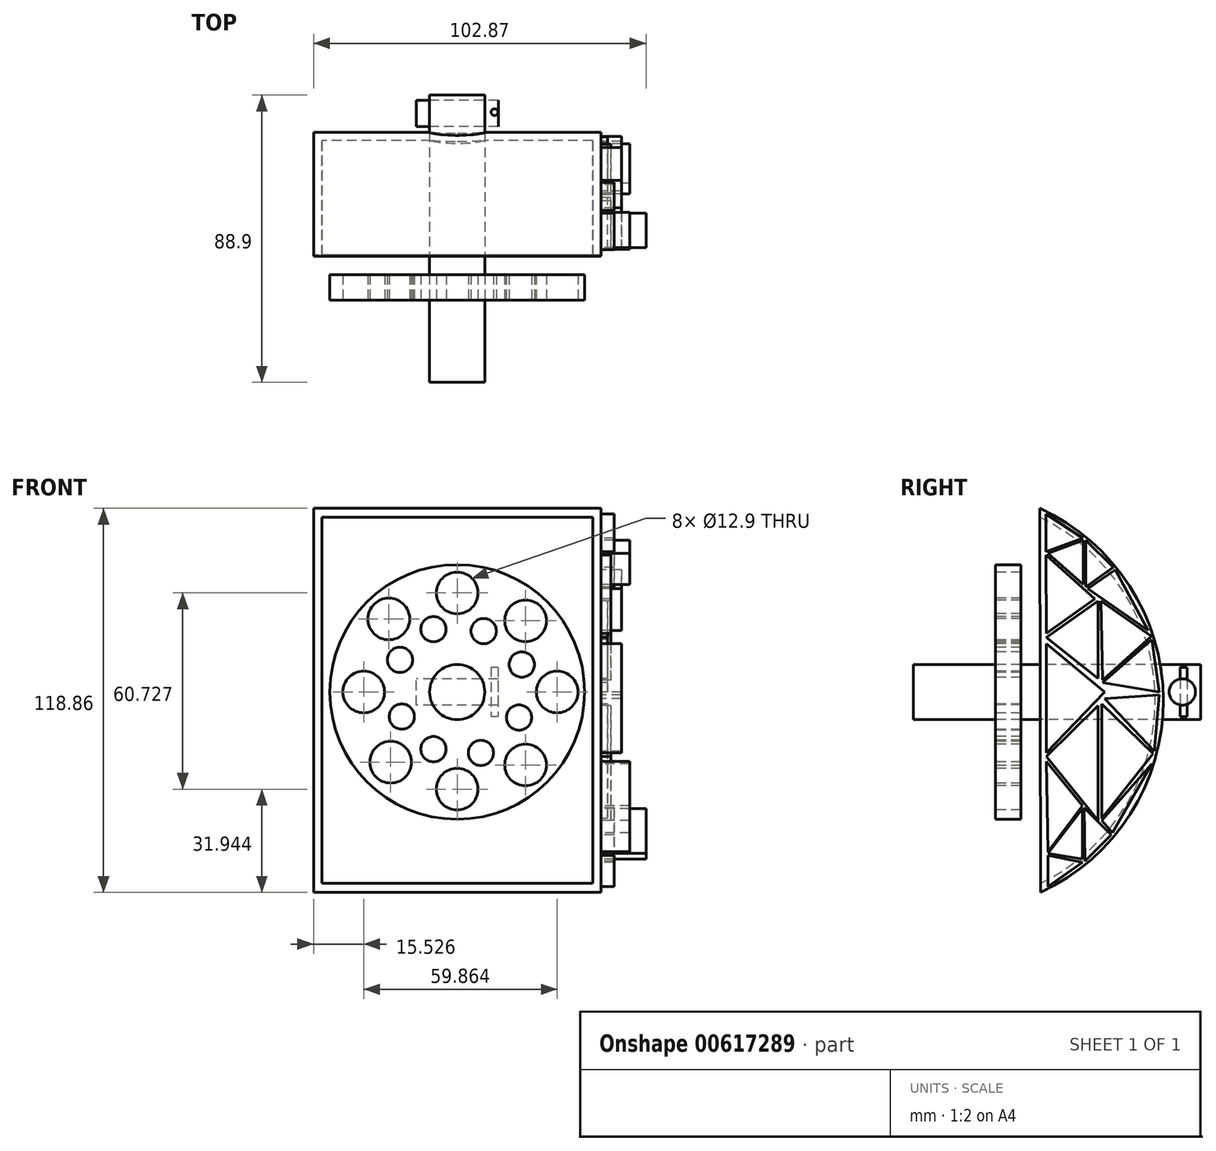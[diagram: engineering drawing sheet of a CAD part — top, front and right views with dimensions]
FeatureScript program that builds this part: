
annotation { "Feature Type Name" : "Feature", "Feature Type Description" : "" }
export const myFeature = defineFeature(function(context is Context, id is Id, definition is map)
    precondition{}
    {
        {
            var Q0;
            Q0=qCreatedBy(makeId("Right.planeOp"),FACE);
            var sketch = newSketch(context, id + "F0", { "sketchPlane" : qUnion([Q0])});
            skArc(sketch, "E0", {"start": v(13.96, -62.02) * mm, "mid": v(51.96, -2.5) * mm, "end": v(13.67, 56.84) * mm});
            skLineSegment(sketch, "E1", {"start": v(13.67, 56.84) * mm, "end": v(13.96, -62.02) * mm});
            skSolve(sketch);
        }
        {
            var Q0;
            Q0 = qSketchRegion(id + "F0", true);
            extrude(context, id + "F1", {"entities" : qUnion([Q0]), "endBound" : BoundingType.SYMMETRIC, "depth" : 88.9 * mm, "offsetDistance" : 25.4 * mm});
        }
        {
            var Q0;
            Q0=makeQuery(id+"F1.opExtrude","SWEPT_FACE",FACE,{"disambiguationData":[OSD([sQuery(id+"F0.wireOp",EDGE,"E1")])]});
            shell(context, id + "F2", {"entities" : qUnion([Q0]), "thickness" : 2.54 * mm});
        }
        {
            var Q0;
            Q0=makeQuery(id+"F1.opExtrude","CAP_FACE",FACE,{"disambiguationData":[OSD([sQuery(id+"F0.wireOp",EDGE,"E0"),sQuery(id+"F0.wireOp",EDGE,"E1")])],"isStart":false});
            var sketch = newSketch(context, id + "F3", { "sketchPlane" : qUnion([Q0])});
            skLineSegment(sketch, "E2", {"start": v(15.74, 14.93) * mm, "end": v(15.82, -18.86) * mm});
            skLineSegment(sketch, "E3", {"start": v(15.82, -18.86) * mm, "end": v(33.85, 0) * mm});
            skLineSegment(sketch, "E4", {"start": v(33.85, 0) * mm, "end": v(15.74, 14.93) * mm});
            skLineSegment(sketch, "E5", {"start": v(15.74, 18.18) * mm, "end": v(15.68, 42.4) * mm});
            skLineSegment(sketch, "E6", {"start": v(15.68, 42.4) * mm, "end": v(30.8, 28.76) * mm});
            skLineSegment(sketch, "E7", {"start": v(30.8, 28.76) * mm, "end": v(15.74, 18.18) * mm});
            skLineSegment(sketch, "E8", {"start": v(15.74, 16.92) * mm, "end": v(31.8, 28.21) * mm});
            skLineSegment(sketch, "E9", {"start": v(31.8, 28.21) * mm, "end": v(31.8, 4.19) * mm});
            skLineSegment(sketch, "E10", {"start": v(31.8, 4.19) * mm, "end": v(15.74, 16.92) * mm});
            skLineSegment(sketch, "E11", {"start": v(15.68, 43.45) * mm, "end": v(15.68, 55.04) * mm});
            skLineSegment(sketch, "E12", {"start": v(15.68, 55.04) * mm, "end": v(27, 47.62) * mm});
            skLineSegment(sketch, "E13", {"start": v(27, 47.62) * mm, "end": v(15.68, 43.45) * mm});
            skLineSegment(sketch, "E14", {"start": v(16.32, 42.93) * mm, "end": v(27.2, 46.95) * mm});
            skLineSegment(sketch, "E15", {"start": v(16.32, 42.93) * mm, "end": v(27.2, 33.3) * mm});
            skLineSegment(sketch, "E16", {"start": v(27.2, 33.3) * mm, "end": v(27.2, 46.95) * mm});
            skLineSegment(sketch, "E17", {"start": v(27.89, 46.95) * mm, "end": v(27.89, 32.54) * mm});
            skLineSegment(sketch, "E18", {"start": v(27.89, 32.54) * mm, "end": v(36.49, 38.62) * mm});
            skLineSegment(sketch, "E19", {"start": v(36.49, 38.62) * mm, "end": v(27.89, 46.95) * mm});
            skLineSegment(sketch, "E20", {"start": v(15.82, -20.01) * mm, "end": v(31.8, -4.22) * mm});
            skLineSegment(sketch, "E21", {"start": v(31.8, -4.22) * mm, "end": v(31.8, -39.8) * mm});
            skLineSegment(sketch, "E22", {"start": v(31.8, -39.8) * mm, "end": v(15.82, -20.01) * mm});
            skLineSegment(sketch, "E23", {"start": v(15.82, -21.43) * mm, "end": v(16.32, -49.42) * mm});
            skLineSegment(sketch, "E24", {"start": v(15.82, -21.43) * mm, "end": v(26.9, -35.15) * mm});
            skLineSegment(sketch, "E25", {"start": v(26.9, -35.15) * mm, "end": v(16.32, -49.42) * mm});
            skLineSegment(sketch, "E26", {"start": v(16.32, -50.52) * mm, "end": v(16.32, -60.2) * mm});
            skLineSegment(sketch, "E27", {"start": v(16.32, -60.2) * mm, "end": v(26.9, -52.7) * mm});
            skLineSegment(sketch, "E28", {"start": v(26.9, -52.7) * mm, "end": v(16.32, -50.52) * mm});
            skLineSegment(sketch, "E29", {"start": v(16.32, -49.9) * mm, "end": v(26.9, -36.05) * mm});
            skLineSegment(sketch, "E30", {"start": v(26.9, -36.05) * mm, "end": v(26.9, -51.68) * mm});
            skLineSegment(sketch, "E31", {"start": v(16.32, -49.9) * mm, "end": v(26.9, -51.68) * mm});
            skLineSegment(sketch, "E32", {"start": v(27.45, -35.79) * mm, "end": v(27.74, -52.3) * mm});
            skLineSegment(sketch, "E33", {"start": v(27.74, -52.3) * mm, "end": v(35.8, -44.17) * mm});
            skLineSegment(sketch, "E34", {"start": v(35.8, -44.17) * mm, "end": v(27.45, -35.79) * mm});
            skLineSegment(sketch, "E35", {"start": v(32.7, 28.21) * mm, "end": v(33.12, 3.7) * mm});
            skLineSegment(sketch, "E36", {"start": v(33.12, 3.7) * mm, "end": v(48.31, 17.27) * mm});
            skLineSegment(sketch, "E37", {"start": v(48.31, 17.27) * mm, "end": v(32.7, 28.21) * mm});
            skLineSegment(sketch, "E38", {"start": v(28.62, 32.03) * mm, "end": v(47.23, 19) * mm});
            skLineSegment(sketch, "E39", {"start": v(47.23, 19) * mm, "end": v(37.12, 37.78) * mm});
            skLineSegment(sketch, "E40", {"start": v(37.12, 37.78) * mm, "end": v(28.62, 32.03) * mm});
            skLineSegment(sketch, "E41", {"start": v(32.9, -3.7) * mm, "end": v(32.9, -39.13) * mm});
            skPoint(sketch, "E41.startSnap0", {"position": v(32.9, 15.95) * mm});
            skLineSegment(sketch, "E42", {"start": v(32.9, -39.13) * mm, "end": v(48.83, -19.04) * mm});
            skLineSegment(sketch, "E43", {"start": v(48.83, -19.04) * mm, "end": v(32.9, -3.7) * mm});
            skLineSegment(sketch, "E44", {"start": v(32.9, -39.83) * mm, "end": v(36.2, -43.52) * mm});
            skLineSegment(sketch, "E45", {"start": v(36.2, -43.52) * mm, "end": v(48.43, -22.25) * mm});
            skLineSegment(sketch, "E46", {"start": v(48.43, -22.25) * mm, "end": v(32.9, -39.83) * mm});
            skLineSegment(sketch, "E47", {"start": v(33.12, 2.9) * mm, "end": v(48.39, 16.17) * mm});
            skLineSegment(sketch, "E48", {"start": v(48.39, 16.17) * mm, "end": v(50.63, 0) * mm});
            skLineSegment(sketch, "E49", {"start": v(50.63, 0) * mm, "end": v(33.12, 2.9) * mm});
            skLineSegment(sketch, "E50", {"start": v(33.85, -2.04) * mm, "end": v(50.69, -0.9) * mm});
            skLineSegment(sketch, "E51", {"start": v(50.69, -0.9) * mm, "end": v(49.11, -18.32) * mm});
            skLineSegment(sketch, "E52", {"start": v(49.11, -18.32) * mm, "end": v(33.85, -2.04) * mm});
            skSolve(sketch);
        }
        {
            var Q0;
            Q0=makeQuery(id+"F3.imprint","IMPRINT",FACE,{"disambiguationData":[TD([[makeQuery(id+"F3.imprint","IMPRINT",EDGE,{"derivedFrom":sQuery(id+"F3.wireOp",EDGE,"E35")}),1.0]])]});
            var Q1;
            Q1=makeQuery(id+"F3.imprint","IMPRINT",FACE,{"disambiguationData":[TD([[makeQuery(id+"F3.imprint","IMPRINT",EDGE,{"derivedFrom":sQuery(id+"F3.wireOp",EDGE,"E5")}),-1.0]])]});
            var Q2;
            Q2=makeQuery(id+"F3.imprint","IMPRINT",FACE,{"disambiguationData":[TD([[makeQuery(id+"F3.imprint","IMPRINT",EDGE,{"derivedFrom":sQuery(id+"F3.wireOp",EDGE,"E20")}),-1.0]])]});
            var Q3;
            Q3=makeQuery(id+"F3.imprint","IMPRINT",FACE,{"disambiguationData":[TD([[makeQuery(id+"F3.imprint","IMPRINT",EDGE,{"derivedFrom":sQuery(id+"F3.wireOp",EDGE,"E50")}),-1.0]])]});
            extrude(context, id + "F4", {"entities" : qUnion([Q0, Q1, Q2, Q3]), "operationType" : NewBodyOperationType.ADD, "depth" : 3.05 * mm, "offsetDistance" : 25.4 * mm});
        }
        {
            var Q0;
            Q0=makeQuery(id+"F3.imprint","IMPRINT",FACE,{"disambiguationData":[TD([[makeQuery(id+"F3.imprint","IMPRINT",EDGE,{"derivedFrom":sQuery(id+"F3.wireOp",EDGE,"E8")}),-1.0]])]});
            var Q1;
            Q1=makeQuery(id+"F3.imprint","IMPRINT",FACE,{"disambiguationData":[TD([[makeQuery(id+"F3.imprint","IMPRINT",EDGE,{"derivedFrom":sQuery(id+"F3.wireOp",EDGE,"E47")}),-1.0]])]});
            var Q2;
            Q2=makeQuery(id+"F3.imprint","IMPRINT",FACE,{"disambiguationData":[TD([[makeQuery(id+"F3.imprint","IMPRINT",EDGE,{"derivedFrom":sQuery(id+"F3.wireOp",EDGE,"E41")}),1.0]])]});
            extrude(context, id + "F5", {"entities" : qUnion([Q0, Q1, Q2]), "operationType" : NewBodyOperationType.ADD, "depth" : 2.03 * mm, "offsetDistance" : 25.4 * mm});
        }
        {
            var Q0;
            Q0=qCreatedBy(makeId("Front.planeOp"),FACE);
            var sketch = newSketch(context, id + "F6", { "sketchPlane" : qUnion([Q0])});
            skCircle(sketch, "E53", {"center": v(0, 0) * mm, "radius": 8.59 * mm});
            skSolve(sketch);
        }
        {
            var Q0;
            Q0 = qSketchRegion(id + "F6", true);
            extrude(context, id + "F7", {"entities" : qUnion([Q0]), "operationType" : NewBodyOperationType.REMOVE, "oppositeDirection" : true, "depth" : 111.76 * mm, "offsetDistance" : 25.4 * mm});
        }
        {
            var Q0;
            Q0=qCreatedBy(makeId("Front.planeOp"),FACE);
            var sketch = newSketch(context, id + "F8", { "sketchPlane" : qUnion([Q0])});
            skCircle(sketch, "E54", {"center": v(0, 0) * mm, "radius": 39.4 * mm});
            skCircle(sketch, "E55", {"center": v(0, -30.08) * mm, "radius": 6.45 * mm});
            skCircle(sketch, "E56", {"center": v(30.94, 0) * mm, "radius": 6.45 * mm});
            skCircle(sketch, "E57", {"center": v(0, 30.65) * mm, "radius": 6.45 * mm});
            skCircle(sketch, "E58", {"center": v(-28.92, 0) * mm, "radius": 6.45 * mm});
            skCircle(sketch, "E59", {"center": v(21.15, -22.6) * mm, "radius": 6.45 * mm});
            skCircle(sketch, "E60", {"center": v(-20.58, -21.73) * mm, "radius": 6.45 * mm});
            skCircle(sketch, "E61", {"center": v(-21.15, 22.6) * mm, "radius": 6.45 * mm});
            skCircle(sketch, "E62", {"center": v(21.15, 22.02) * mm, "radius": 6.45 * mm});
            skCircle(sketch, "E63", {"center": v(-7.34, 19.43) * mm, "radius": 3.91 * mm});
            skCircle(sketch, "E64", {"center": v(8.2, 18.85) * mm, "radius": 3.91 * mm});
            skCircle(sketch, "E65", {"center": v(20, 8.5) * mm, "radius": 3.91 * mm});
            skCircle(sketch, "E66", {"center": v(19.14, -7.91) * mm, "radius": 3.91 * mm});
            skCircle(sketch, "E67", {"center": v(7.34, -18.85) * mm, "radius": 3.91 * mm});
            skCircle(sketch, "E68", {"center": v(-17.12, -7.63) * mm, "radius": 3.91 * mm});
            skCircle(sketch, "E69", {"center": v(-17.7, 9.93) * mm, "radius": 3.91 * mm});
            skCircle(sketch, "E70", {"center": v(-7.34, -17.7) * mm, "radius": 3.91 * mm});
            skCircle(sketch, "E71", {"center": v(0, 0) * mm, "radius": 8.54 * mm});
            skSolve(sketch);
        }
        {
            var Q0;
            Q0 = qSketchRegion(id + "F8", true);
            extrude(context, id + "F9", {"entities" : qUnion([Q0]), "oppositeDirection" : true, "depth" : 7.87 * mm, "offsetDistance" : 25.4 * mm});
        }
        {
            var Q0;
            Q0=makeQuery(id+"F3.imprint","IMPRINT",FACE,{"disambiguationData":[TD([[makeQuery(id+"F3.imprint","IMPRINT",EDGE,{"derivedFrom":sQuery(id+"F3.wireOp",EDGE,"E17")}),1.0]])]});
            var Q1;
            Q1=makeQuery(id+"F3.imprint","IMPRINT",FACE,{"disambiguationData":[TD([[makeQuery(id+"F3.imprint","IMPRINT",EDGE,{"derivedFrom":sQuery(id+"F3.wireOp",EDGE,"E32")}),1.0]])]});
            var Q2;
            Q2=makeQuery(id+"F3.imprint","IMPRINT",FACE,{"disambiguationData":[TD([[makeQuery(id+"F3.imprint","IMPRINT",EDGE,{"derivedFrom":sQuery(id+"F3.wireOp",EDGE,"E11")}),-1.0]])]});
            var Q3;
            Q3=makeQuery(id+"F3.imprint","IMPRINT",FACE,{"disambiguationData":[TD([[makeQuery(id+"F3.imprint","IMPRINT",EDGE,{"derivedFrom":sQuery(id+"F3.wireOp",EDGE,"E26")}),1.0]])]});
            extrude(context, id + "F10", {"entities" : qUnion([Q0, Q1, Q2, Q3]), "operationType" : NewBodyOperationType.ADD, "depth" : 4.06 * mm, "offsetDistance" : 25.4 * mm});
        }
        {
            var Q0;
            Q0=makeQuery(id+"F3.imprint","IMPRINT",FACE,{"disambiguationData":[TD([[makeQuery(id+"F3.imprint","IMPRINT",EDGE,{"derivedFrom":sQuery(id+"F3.wireOp",EDGE,"E2")}),1.0]])]});
            var Q1;
            Q1=makeQuery(id+"F3.imprint","IMPRINT",FACE,{"disambiguationData":[TD([[makeQuery(id+"F3.imprint","IMPRINT",EDGE,{"derivedFrom":sQuery(id+"F3.wireOp",EDGE,"E38")}),1.0]])]});
            var Q2;
            Q2=makeQuery(id+"F3.imprint","IMPRINT",FACE,{"disambiguationData":[TD([[makeQuery(id+"F3.imprint","IMPRINT",EDGE,{"derivedFrom":sQuery(id+"F3.wireOp",EDGE,"E50")}),-1.0]])]});
            extrude(context, id + "F11", {"entities" : qUnion([Q0, Q1, Q2]), "operationType" : NewBodyOperationType.ADD, "depth" : 6.35 * mm, "offsetDistance" : 25.4 * mm});
        }
        {
            var Q0;
            Q0=makeQuery(id+"F3.imprint","IMPRINT",FACE,{"disambiguationData":[TD([[makeQuery(id+"F3.imprint","IMPRINT",EDGE,{"derivedFrom":sQuery(id+"F3.wireOp",EDGE,"E14")}),-1.0]])]});
            var Q1;
            Q1=makeQuery(id+"F3.imprint","IMPRINT",FACE,{"disambiguationData":[TD([[makeQuery(id+"F3.imprint","IMPRINT",EDGE,{"derivedFrom":sQuery(id+"F3.wireOp",EDGE,"E23")}),1.0]])]});
            var Q2;
            Q2=makeQuery(id+"F3.imprint","IMPRINT",FACE,{"disambiguationData":[TD([[makeQuery(id+"F3.imprint","IMPRINT",EDGE,{"derivedFrom":sQuery(id+"F3.wireOp",EDGE,"E44")}),1.0]])]});
            extrude(context, id + "F12", {"entities" : qUnion([Q0, Q1, Q2]), "operationType" : NewBodyOperationType.ADD, "depth" : 8.9 * mm, "offsetDistance" : 25.4 * mm});
        }
        {
            var Q0;
            Q0=makeQuery(id+"F3.imprint","IMPRINT",FACE,{"disambiguationData":[TD([[makeQuery(id+"F3.imprint","IMPRINT",EDGE,{"derivedFrom":sQuery(id+"F3.wireOp",EDGE,"E29")}),-1.0]])]});
            extrude(context, id + "F13", {"entities" : qUnion([Q0]), "operationType" : NewBodyOperationType.ADD, "depth" : 13.97 * mm, "offsetDistance" : 25.4 * mm});
        }
        {
            var Q0;
            Q0=qCreatedBy(makeId("Front.planeOp"),FACE);
            var sketch = newSketch(context, id + "F14", { "sketchPlane" : qUnion([Q0])});
            skCircle(sketch, "E72", {"center": v(0, 0) * mm, "radius": 8.54 * mm});
            skSolve(sketch);
        }
        {
            var Q0;
            Q0 = qSketchRegion(id + "F14", true);
            extrude(context, id + "F15", {"entities" : qUnion([Q0]), "oppositeDirection" : true, "depth" : 63.5 * mm, "offsetDistance" : 25.4 * mm, "hasSecondDirection" : true, "secondDirectionOppositeDirection" : false, "secondDirectionDepth" : 25.4 * mm});
        }
        {
            var Q0;
            Q0=qCreatedBy(makeId("Right.planeOp"),FACE);
            var sketch = newSketch(context, id + "F16", { "sketchPlane" : qUnion([Q0])});
            skCircle(sketch, "E73", {"center": v(57.83, 0) * mm, "radius": 4.08 * mm});
            skSolve(sketch);
        }
        {
            var Q0;
            Q0 = qSketchRegion(id + "F16", true);
            extrude(context, id + "F17", {"entities" : qUnion([Q0]), "endBound" : BoundingType.SYMMETRIC, "depth" : 25.4 * mm, "offsetDistance" : 25.4 * mm});
        }
        {
            var Q0;
            Q0=qCreatedBy(makeId("Top.planeOp"),FACE);
            var sketch = newSketch(context, id + "F18", { "sketchPlane" : qUnion([Q0])});
            skCircle(sketch, "E74", {"center": v(11.55, 58.21) * mm, "radius": 1.04 * mm});
            skSolve(sketch);
        }
        {
            var Q0;
            Q0 = qSketchRegion(id + "F18", true);
            extrude(context, id + "F19", {"entities" : qUnion([Q0]), "depth" : 7.62 * mm, "offsetDistance" : 25.4 * mm, "hasSecondDirection" : true, "secondDirectionOppositeDirection" : true, "secondDirectionDepth" : 7.62 * mm});
        }
    });
